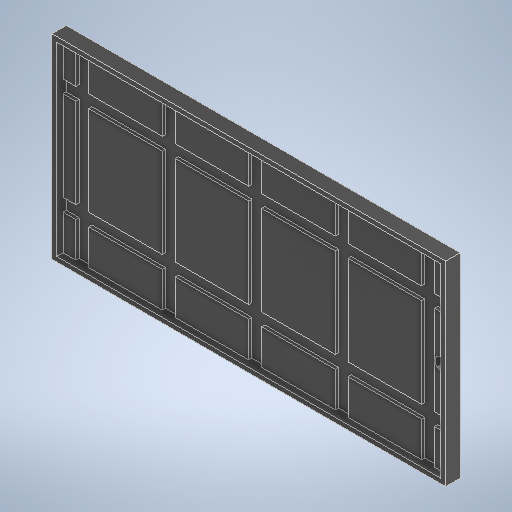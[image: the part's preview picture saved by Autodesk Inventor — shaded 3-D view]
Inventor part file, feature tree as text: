
AUTODESK INVENTOR PART (.ipt)
format: ipt  version: 2025 (Build 290162000, 162)  size: 340,480 bytes
history: native  units: in
note: dims shown in document units (in); Inventor stores cm internally (conversion verified against a paired STEP export)
features: extrude x5, sketch x5
ambient origin geometry x8: Origin, YZ Plane, XZ Plane, XY Plane, X Axis, Y Axis, Z Axis, Center Point
bodies: Solid1 (feature_tree)
feature tree (10):
  extrude  "Extrusion1"  Depth=48.4252in
  extrude  "Extrusion2"  Depth=47.2441in
  extrude  "Extrusion3"  Depth=0.7874in TaperAngle=0.0deg
  extrude  "Extrusion4"  Depth=1.5748in
  extrude  "Extrusion5"  Depth=1.5748in
  sketch  "Sketch1"  dims[d0=24.0157in d1=48.4252in]
  sketch  "Sketch2"  dims[d2=1.7717in d3=0.0in d4=47.2441in]
  sketch  "Sketch3"  dims[d5=22.8346in d6=0.7874in d7=0.0in]
  sketch  "Sketch4"  dims[d8=22.8346in d9=1.5748in]
  sketch  "Sketch5"  dims[d10=9.8425in d11=1.5748in d12=1.5748in d13=9.8425in d14=1.5748in d15=9.0551in d16=22.8346in d17=1.5748in d18=9.0551in d19=0.3937in d20=0.0in d21=5.5118in d22=5.5118in d23=1.5748in d24=1.5748in d25=47.2441in d26=0.3937in d27=0.0in d28=1.4567in d29=22.8346in d30=1.4567in d31=0.0in]
